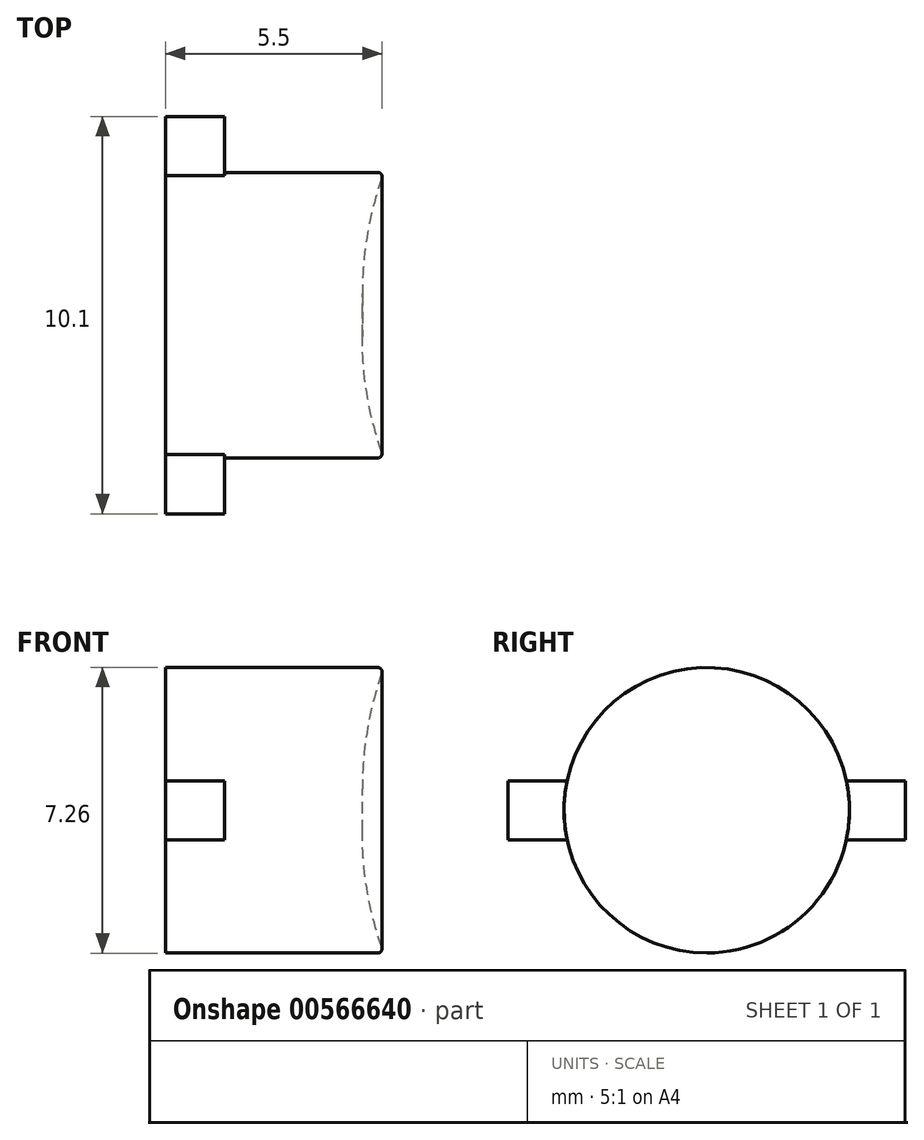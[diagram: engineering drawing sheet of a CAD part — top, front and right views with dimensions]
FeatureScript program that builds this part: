
annotation { "Feature Type Name" : "Feature", "Feature Type Description" : "" }
export const myFeature = defineFeature(function(context is Context, id is Id, definition is map)
    precondition{}
    {
        {
            var Q0;
            Q0=qCreatedBy(makeId("Right.planeOp"),FACE);
            var sketch = newSketch(context, id + "F0", { "sketchPlane" : qUnion([Q0])});
            skCircle(sketch, "E0", {"center": v(0, 0) * mm, "radius": 3.62 * mm});
            skSolve(sketch);
        }
        {
            var Q0;
            Q0=makeQuery(id+"F0.imprint","IMPRINT",FACE,{"disambiguationData":[TD([[makeQuery(id+"F0.imprint","IMPRINT",EDGE,{"derivedFrom":sQuery(id+"F0.wireOp",EDGE,"E0")}),1.0]])]});
            extrude(context, id + "F1", {"entities" : qUnion([Q0]), "endBound" : BoundingType.SYMMETRIC, "depth" : 5.5 * mm, "offsetDistance" : 25 * mm});
        }
        {
            var Q0;
            Q0=makeQuery(id+"F1.opExtrude","CAP_FACE",FACE,{"disambiguationData":[OSD([sQuery(id+"F0.wireOp",EDGE,"E0")])],"isStart":true});
            var sketch = newSketch(context, id + "F2", { "sketchPlane" : qUnion([Q0])});
            skLineSegment(sketch, "E1.left", {"start": v(5.05, -0.75) * mm, "end": v(5.05, 0.75) * mm});
            skLineSegment(sketch, "E2.left", {"start": v(-5.05, 0.75) * mm, "end": v(-5.05, -0.75) * mm});
            skLineSegment(sketch, "E3", {"start": v(5.05, 0.75) * mm, "end": v(3.55, 0.75) * mm});
            skLineSegment(sketch, "E4", {"start": v(5.05, -0.75) * mm, "end": v(3.55, -0.75) * mm});
            skArc(sketch, "E5", {"start": v(-3.55, 0.75) * mm, "mid": v(-3.63, 0) * mm, "end": v(-3.55, -0.75) * mm});
            skLineSegment(sketch, "E6", {"start": v(-5.05, 0.75) * mm, "end": v(-3.55, 0.75) * mm});
            skLineSegment(sketch, "E7", {"start": v(-5.05, -0.75) * mm, "end": v(-3.55, -0.75) * mm});
            skArc(sketch, "E8.trimOffspring", {"start": v(3.55, -0.75) * mm, "mid": v(3.63, 0) * mm, "end": v(3.55, 0.75) * mm});
            skPoint(sketch, "E9", {"position": v(5.05, 0) * mm});
            skPoint(sketch, "E10", {"position": v(-5.05, 0) * mm});
            skSolve(sketch);
        }
        {
            var Q0;
            Q0=qSketchRegion(id+"F2",true);
            extrude(context, id + "F3", {"entities" : qUnion([Q0]), "operationType" : NewBodyOperationType.ADD, "oppositeDirection" : true, "depth" : 1.5 * mm, "offsetDistance" : 25 * mm});
        }
        {
            var Q0;
            Q0=makeQuery(id+"F1.opExtrude","CAP_FACE",FACE,{"disambiguationData":[OSD([sQuery(id+"F0.wireOp",EDGE,"E0")])],"isStart":false});
            var sketch = newSketch(context, id + "F4", { "sketchPlane" : qUnion([Q0])});
            skCircle(sketch, "E11", {"center": v(0, 0) * mm, "radius": 3.5 * mm});
            skSolve(sketch);
        }
        {
            var Q0;
            Q0=qSketchRegion(id+"F4",true);
            extrude(context, id + "F5", {"entities" : qUnion([Q0]), "operationType" : NewBodyOperationType.REMOVE, "oppositeDirection" : true, "depth" : .5 * mm, "offsetDistance" : 25 * mm});
        }
        {
            var Q0;
            Q0=makeQuery(id+"F5.boolean.opBoolean","COPY",FACE,{"derivedFrom":makeQuery(id+"F5.opExtrude","CAP_FACE",FACE,{"disambiguationData":[OSD([sQuery(id+"F4.wireOp",EDGE,"E11")])],"isStart":false})});
            fillet(context, id + "F6", {"entities" : qUnion([Q0]), "radius" : 9 * mm, "tangentPropagation" : true, "allowEdgeOverflow" : false});
        }
        {
            var Q0;
            Q0=makeQuery(id+"F6.opFillet","BLEND_EDGE",EDGE,{"blendedFrom":[makeQuery(id+"F5.boolean.opBoolean","COPY",EDGE,{"derivedFrom":makeQuery(id+"F5.opExtrude","CAP_EDGE",EDGE,{"disambiguationData":[OSD([sQuery(id+"F4.wireOp",EDGE,"E11")])],"isStart":false})}),makeQuery(id+"F1.opExtrude","CAP_FACE",FACE,{"disambiguationData":[OSD([sQuery(id+"F0.wireOp",EDGE,"E0")])],"isStart":false})],"blendedInto":[makeQuery(id+"F1.opExtrude","CAP_FACE",FACE,{"disambiguationData":[OSD([sQuery(id+"F0.wireOp",EDGE,"E0")])],"isStart":false})]});
            var Q1;
            Q1=makeQuery(id+"F1.opExtrude","CAP_EDGE",EDGE,{"disambiguationData":[OSD([sQuery(id+"F0.wireOp",EDGE,"E0")])],"isStart":false});
            fillet(context, id + "F7", {"entities" : qUnion([Q0, Q1]), "radius" : .1 * mm, "tangentPropagation" : true, "allowEdgeOverflow" : false});
        }
    });
